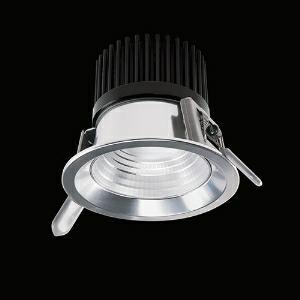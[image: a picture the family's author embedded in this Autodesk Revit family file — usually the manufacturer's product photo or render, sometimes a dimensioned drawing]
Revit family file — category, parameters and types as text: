
# Revit family: spectral_myral_myral_4500-830-m
name_source: partatom
category: Lighting Fixtures
revit_build: Autodesk Revit 2016 (Build: 20150220_1215(x64)
units: mm (PartAtom-declared; Revit-internal decimal feet)

## family parameters
Cut with Voids When Loaded = No
Host = Face
Light Source = No
Part Type = Normal
Room Calculation Point = No
Round Connector Dimension = Use Diameter
Shared = No

## types (1)
- SPECTRAL MYRAL (1 x )
    Apparent Load = 0 VA
    Approval mark = CE
    CIE Flux Codes = 82 99 100 100 100
    Control Gear = Electronic transformer
    Default Elevation = 1800 mm
    Description = SPG0320182
MYRAL recessed spot

Design:
    Height = 0 mm  [stored 0 ft]
    Lamp = 1 x
    Lamp count = 1
    Length = 120 mm
    Luminous efficacy = 0 lm/W
    Manufacturer = Ridi
    ModVariant = No
    Model = MYRAL 4500-830-M
    Mounting Place = Ceiling
    Mounting Type = Recessed
    Number of Poles = 1
    OnlyDefault = Yes
    Power Factor = 1
    Product Name = SPECTRAL MYRAL
    Product group = Downlight recessed
    ProductGroupID = 400
    Protection Class = Protection class
    Protection Degree = IP 20
    RlxData = <blob elided: 38673 chars, md5=3279361b>
    Socket = socket
    Standby Power = 0 W
    System Light Flux = 0 lm
    System Power = 0 W
    Type Image = myral_04.jpg
    URL = http://reluxnet.relux.com
    VarID = ---
    Voltage = 0 V
    Weight = 0.00 kg
    Width = 0 mm  [stored 0 ft]

note: [stored X ft] marks values corroborated as IEEE doubles in the binary element streams (Revit-internal decimal feet)

## geometry (parser evidence)
native form markers: Sweep x9
no freeform markers — native parametric forms only
